# Revit family: Arper_Catifa53_bench_3133
name_source: partatom
category: Furniture
units: mm (PartAtom-declared; Revit-internal decimal feet)

## family parameters
Always vertical = Yes
Cut with Voids When Loaded = No
OmniClass Number = 23.40.20.00
OmniClass Title = General Furniture and Specialties
Room Calculation Point = No
Shared = No
Work Plane-Based = No

## types (1)
- Arper_Catifa53_bench_3133
    Arper - Shell = Yes
    Arper - Shell 2 = Yes
    Arper - Shell 3 = No
    Arper - Shell 4 = No
    Arper - Shell material = Arper - V12
    Arper - Tablet material = Arper - Steel
    Default Elevation = 0 cm
    Description = Bench with powder-coated metal frame, available in three sizes to 
accommodate two, three or four units fitted with post-consumer recycled material shells 
or powder-coated steel tables.
    Keynote = bench
    Manufacturer = ARPER s.p.a.
    Model = Catifa Bench
    Tablet = No
    Tablet 2 = No
    Tablet 3 = Yes
    Tablet 4 = Yes
    URL = http://www.arper.com
